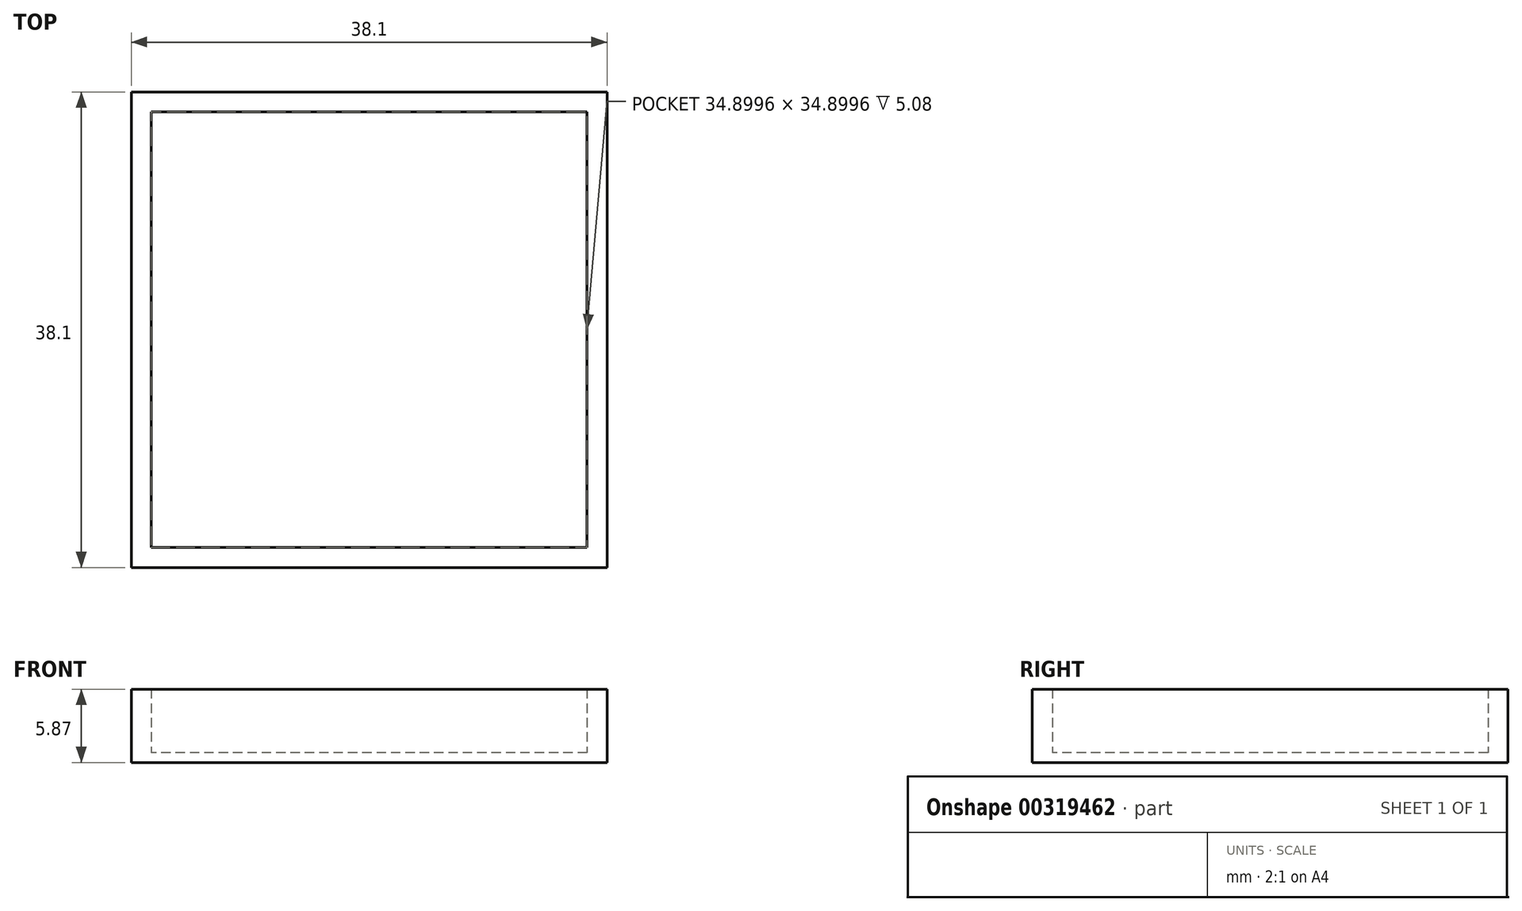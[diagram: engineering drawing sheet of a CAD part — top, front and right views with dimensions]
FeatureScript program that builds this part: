
annotation { "Feature Type Name" : "Feature", "Feature Type Description" : "" }
export const myFeature = defineFeature(function(context is Context, id is Id, definition is map)
    precondition{}
    {
        {
            var Q0;
            Q0=qCreatedBy(makeId("Top.planeOp"),FACE);
            var sketch = newSketch(context, id + "F0", { "sketchPlane" : qUnion([Q0])});
            skLineSegment(sketch, "E0.bottom", {"start": v(-26.37, 17.35) * mm, "end": v(11.73, 17.35) * mm});
            skLineSegment(sketch, "E0.top", {"start": v(-26.37, -20.75) * mm, "end": v(11.73, -20.75) * mm});
            skLineSegment(sketch, "E0.left", {"start": v(-26.37, 17.35) * mm, "end": v(-26.37, -20.75) * mm});
            skLineSegment(sketch, "E0.right", {"start": v(11.73, 17.35) * mm, "end": v(11.73, -20.75) * mm});
            skSolve(sketch);
        }
        {
            var Q0;
            Q0=makeQuery(id+"F0.imprint","IMPRINT",FACE,{"disambiguationData":[TD([[makeQuery(id+"F0.imprint","IMPRINT",EDGE,{"derivedFrom":sQuery(id+"F0.wireOp",EDGE,"E0.bottom")}),-1.0]])]});
            extrude(context, id + "F1", {"entities" : qUnion([Q0]), "depth" : 0.79 * mm, "offsetDistance" : 25.4 * mm});
        }
        {
            var Q0;
            Q0=makeQuery(id+"F1.opExtrude","CAP_FACE",FACE,{"disambiguationData":[OSD([sQuery(id+"F0.wireOp",EDGE,"E0.bottom"),sQuery(id+"F0.wireOp",EDGE,"E0.top"),sQuery(id+"F0.wireOp",EDGE,"E0.left"),sQuery(id+"F0.wireOp",EDGE,"E0.right")])],"isStart":false});
            var sketch = newSketch(context, id + "F2", { "sketchPlane" : qUnion([Q0])});
            skLineSegment(sketch, "E1.0", {"start": v(-24.77, 15.75) * mm, "end": v(-24.77, -19.15) * mm});
            skLineSegment(sketch, "E1.1", {"start": v(10.13, 15.75) * mm, "end": v(-24.77, 15.75) * mm});
            skLineSegment(sketch, "E1.2", {"start": v(10.13, -19.15) * mm, "end": v(10.13, 15.75) * mm});
            skLineSegment(sketch, "E1.3", {"start": v(-24.77, -19.15) * mm, "end": v(10.13, -19.15) * mm});
            skSolve(sketch);
        }
        {
            var Q0;
            Q0=makeQuery(id+"F2.imprint","IMPRINT",FACE,{"disambiguationData":[TD([[makeQuery(id+"F2.imprint","IMPRINT",EDGE,{"derivedFrom":sQuery(id+"F2.wireOp",EDGE,"E1.0")}),-1.0]])]});
            extrude(context, id + "F3", {"entities" : qUnion([Q0]), "operationType" : NewBodyOperationType.ADD, "depth" : 5.08 * mm, "offsetDistance" : 25.4 * mm});
        }
    });
